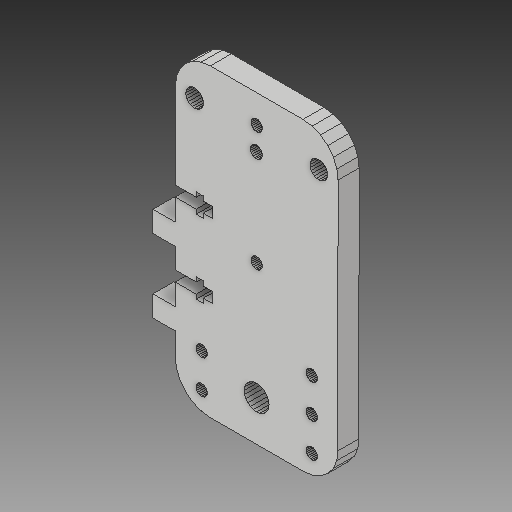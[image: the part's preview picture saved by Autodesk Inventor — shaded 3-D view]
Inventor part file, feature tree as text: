
AUTODESK INVENTOR PART (.ipt)
format: ipt  version: 2018 (Build 220112000, 112)  size: 586,752 bytes
history: native  units: mm
features: other x3, sketch x1
ambient origin geometry x8: Origin, YZ Plane, XZ Plane, XY Plane, X Axis, Y Axis, Z Axis, Center Point
bodies: Solid1 (feature_tree)
feature tree (4):
  other  "Hotend Rear Plate.ipt"
  other  "Solid1::Hotend Rear Plate.ipt"
  other  "TaggingFeature1"
  sketch  "Sketch1"  dims[d0=10.0mm]
